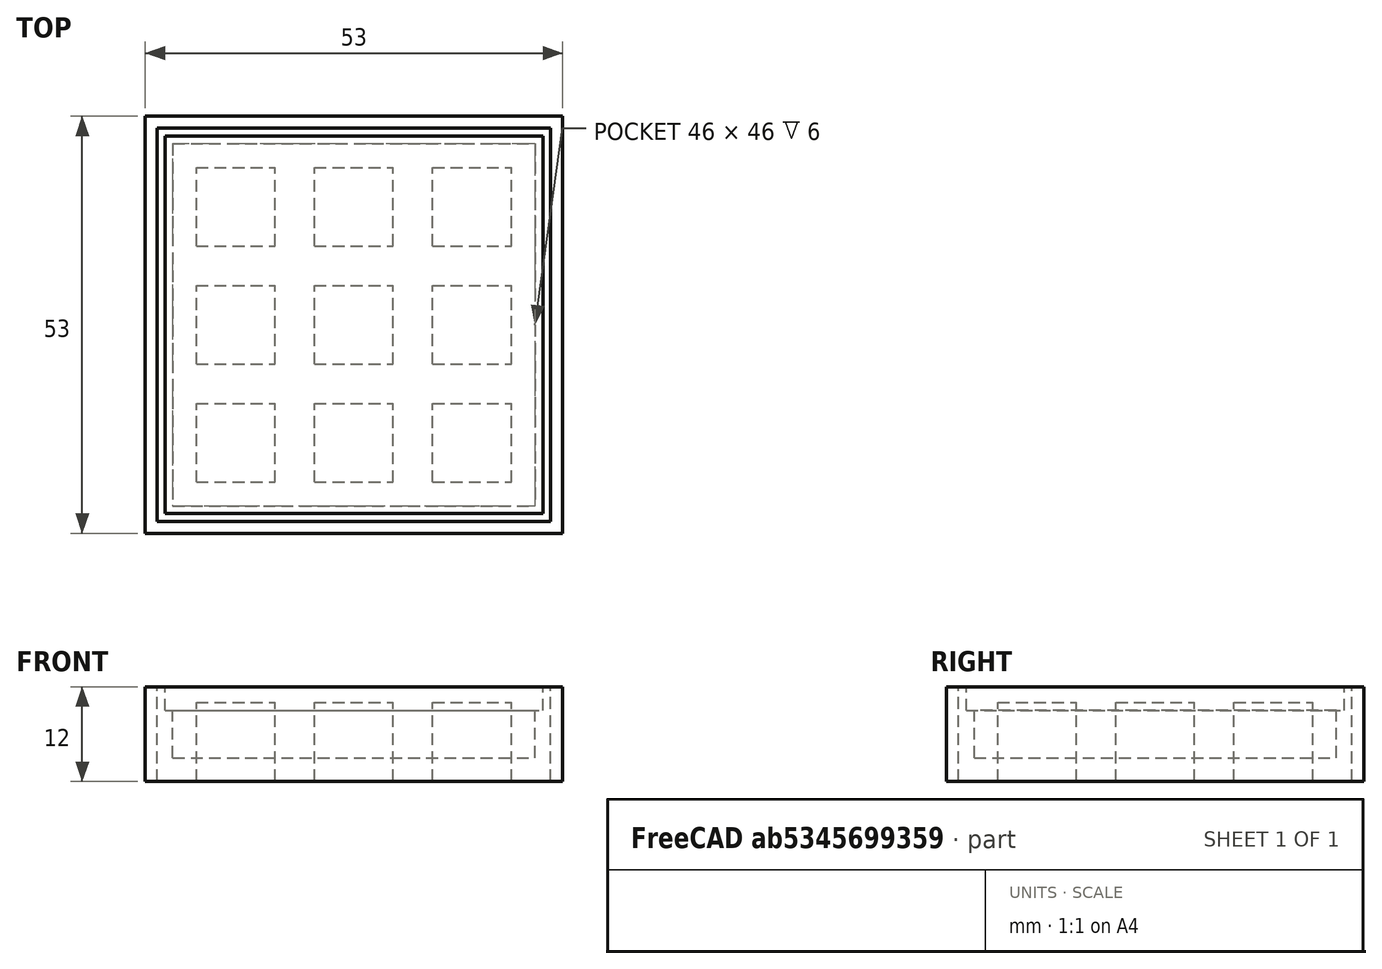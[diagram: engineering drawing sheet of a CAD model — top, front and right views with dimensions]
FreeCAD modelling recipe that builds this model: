
FCSTD DOCUMENT  (FreeCAD 1.0R39109 (Git))
Label: switch-tester
License: All rights reserved
LicenseURL: https://en.wikipedia.org/wiki/All_rights_reserved
objects: Part::Box×14, Part::Cut×2, App::DocumentObjectGroup×1
note: 16 computed .brp shape members not serialized (recipe doc carries the construction recipe); baked Part::Feature solids carry a one-line shape summary decoded from their .brp

FEATURE [Part::Box] Box  label="Cube"
  AttacherType = Attacher::AttachEngine3D
  Height = 9
  Length = 46
  Placement = pos=(0,0,3) rot=(0,0,1;0rad)
  Width = 46
FEATURE [Part::Box] Box001  label="Cube001"
  AttacherType = Attacher::AttachEngine3D
  Height = 10
  Length = 10
  Placement = pos=(3,3,0) rot=(0,0,1;0rad)
  Width = 10
FEATURE [Part::Box] Box002  label="Cube002"
  AttacherType = Attacher::AttachEngine3D
  Height = 10
  Length = 10
  Placement = pos=(18,3,0) rot=(0,0,1;0rad)
  Width = 10
FEATURE [Part::Box] Box003  label="Cube003"
  AttacherType = Attacher::AttachEngine3D
  Height = 10
  Length = 10
  Placement = pos=(33,3,0) rot=(0,0,1;0rad)
  Width = 10
FEATURE [Part::Box] Box004  label="Cube004"
  AttacherType = Attacher::AttachEngine3D
  Height = 10
  Length = 10
  Placement = pos=(3,18,0) rot=(0,0,1;0rad)
  Width = 10
FEATURE [Part::Box] Box005  label="Cube005"
  AttacherType = Attacher::AttachEngine3D
  Height = 10
  Length = 10
  Placement = pos=(18,18,0) rot=(0,0,1;0rad)
  Width = 10
FEATURE [Part::Box] Box006  label="Cube006"
  AttacherType = Attacher::AttachEngine3D
  Height = 10
  Length = 10
  Placement = pos=(33,18,0) rot=(0,0,1;0rad)
  Width = 10
FEATURE [Part::Box] Box007  label="Cube007"
  AttacherType = Attacher::AttachEngine3D
  Height = 10
  Length = 10
  Placement = pos=(3,33,0) rot=(0,0,1;0rad)
  Width = 10
FEATURE [Part::Box] Box008  label="Cube008"
  AttacherType = Attacher::AttachEngine3D
  Height = 10
  Length = 10
  Placement = pos=(18,33,0) rot=(0,0,1;0rad)
  Width = 10
FEATURE [Part::Box] Box009  label="Cube009"
  AttacherType = Attacher::AttachEngine3D
  Height = 10
  Length = 10
  Placement = pos=(33,33,0) rot=(0,0,1;0rad)
  Width = 10
FEATURE [Part::Box] Box010  label="Cube010"
  AttacherType = Attacher::AttachEngine3D
  Height = 12
  Length = 50
  Placement = pos=(-2,-2,0) rot=(0,0,1;0rad)
  Width = 50
FEATURE [App::DocumentObjectGroup] Group  label="Switch Slots"
  Group = -> [Box001,Box002,Box003,Box004,Box005,Box006,Box007,Box008,Box009]
FEATURE [Part::Box] Box011  label="Cube011"
  AttacherType = Attacher::AttachEngine3D
  Height = 3
  Length = 48
  Placement = pos=(-1,-1,9) rot=(0,0,1;0rad)
  Width = 48
FEATURE [Part::Cut] Cut
  Base = -> Box010
  Tool = -> Box
FEATURE [Part::Box] Box012  label="Cube012"
  AttacherType = Attacher::AttachEngine3D
  Height = 3
  Length = 48
  Placement = pos=(-1,-1,9) rot=(0,0,1;0rad)
  Width = 48
FEATURE [Part::Cut] Cut001
  Base = -> Cut
  Tool = -> Box011
FEATURE [Part::Box] Box013  label="Cube013"
  AttacherType = Attacher::AttachEngine3D
  Height = 12
  Length = 53
  Placement = pos=(-3.5,-3.5,0) rot=(0,0,1;0rad)
  Width = 53
